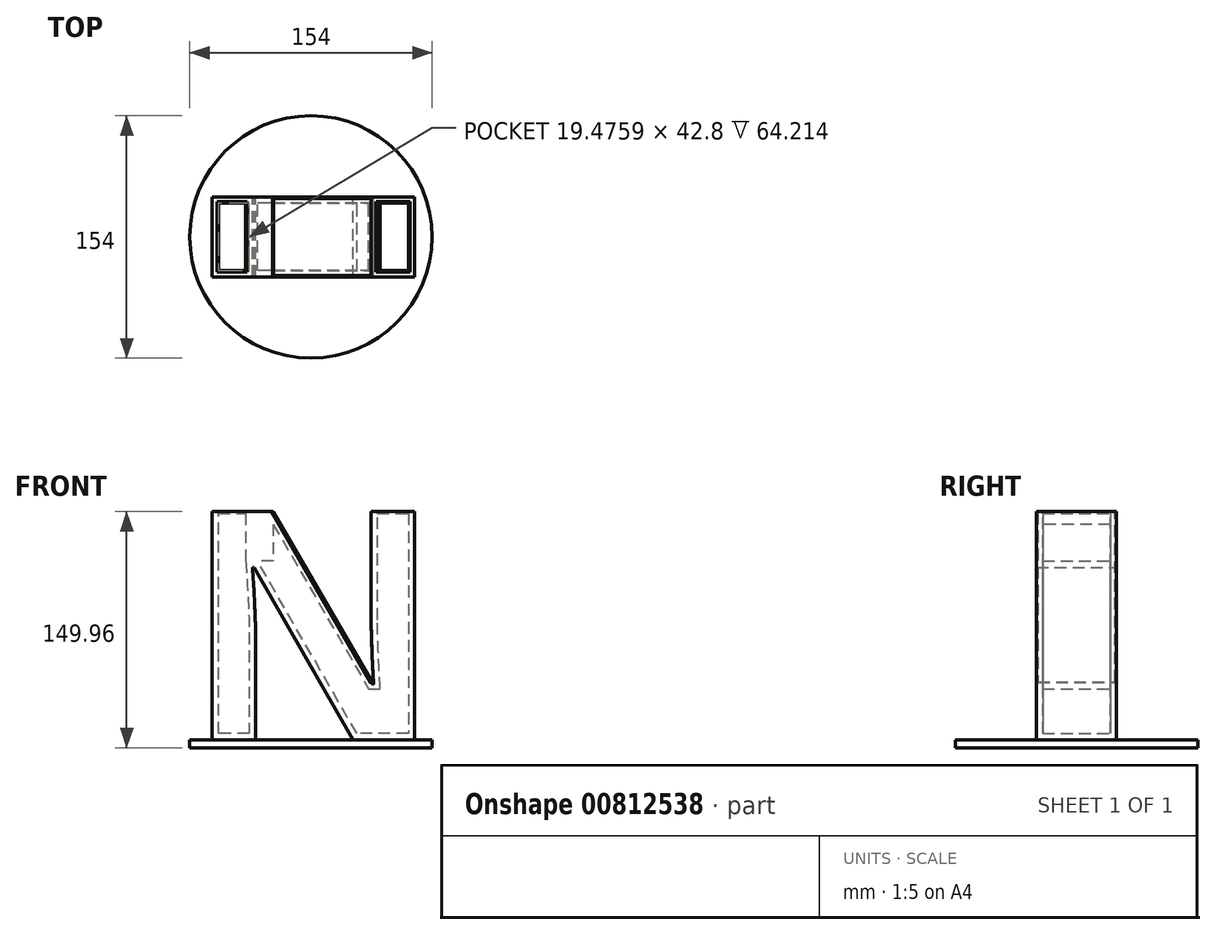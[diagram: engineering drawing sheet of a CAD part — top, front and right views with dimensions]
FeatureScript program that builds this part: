
annotation { "Feature Type Name" : "Feature", "Feature Type Description" : "" }
export const myFeature = defineFeature(function(context is Context, id is Id, definition is map)
    precondition{}
    {
        {
            var Q0;
            Q0=qCreatedBy(makeId("Top.planeOp"),FACE);
            var sketch = newSketch(context, id + "F0", { "sketchPlane" : qUnion([Q0])});
            skCircle(sketch, "E0", {"center": v(0, 0) * mm, "radius": 77 * mm});
            skSolve(sketch);
        }
        {
            var Q0;
            Q0=makeQuery(id+"F0.imprint","IMPRINT",FACE,{"disambiguationData":[TD([[makeQuery(id+"F0.imprint","IMPRINT",EDGE,{"derivedFrom":sQuery(id+"F0.wireOp",EDGE,"E0")}),1.0]])]});
            extrude(context, id + "F1", {"entities" : qUnion([Q0]), "oppositeDirection" : true, "depth" : 5 * mm, "offsetDistance" : 25 * mm});
        }
        {
            var Q0;
            Q0=qCreatedBy(makeId("Front.planeOp"),FACE);
            var sketch = newSketch(context, id + "F2", { "sketchPlane" : qUnion([Q0])});
            skText(sketch, "E1", { "text": "N", "fontName": "OpenSans-Bold.ttf"});
            const initialGuessF2  = {"E1": [-0.08095, 0, 1, 0, 0.1462]};
            skSetInitialGuess(sketch, initialGuessF2);
            skSolve(sketch);
        }
        {
            var Q0;
            Q0 = qSketchRegion(id + "F2", true);
            extrude(context, id + "F3", {"entities" : qUnion([Q0]), "endBound" : BoundingType.SYMMETRIC, "depth" : 50.8 * mm, "offsetDistance" : 25 * mm});
        }
        {
            var Q0;
            Q0=makeQuery(id+"F3.opExtrude","SWEPT_FACE",FACE,{"disambiguationData":[OSD([sQuery(id+"F2.wireOp",EDGE,"E1.sketch_text.stroke-7")])]});
            var Q1;
            Q1=makeQuery(id+"F3.opExtrude","SWEPT_FACE",FACE,{"disambiguationData":[OSD([sQuery(id+"F2.wireOp",EDGE,"E1.sketch_text.stroke-12")])]});
            shell(context, id + "F4", {"entities" : qUnion([Q0, Q1]), "thickness" : 4 * mm});
        }
        {
            var Q0;
            Q0=makeQuery(id+"F4.opShell","OFFSET_FACE",FACE,{"disambiguationData":[OSD([sQuery(id+"F2.wireOp",EDGE,"E1.sketch_text.stroke-2")])]});
            extrude(context, id + "F5", {"entities" : qUnion([Q0]), "operationType" : NewBodyOperationType.ADD, "depth" : 31.3 * mm, "offsetDistance" : 25 * mm});
        }
        {
            var Q0;
            Q0=makeQuery(id+"F5.opExtrude","SWEPT_FACE",FACE,{"disambiguationData":[OSD([sQuery(id+"F2.wireOp",EDGE,"E1.sketch_text.stroke-1"),sQuery(id+"F2.wireOp",EDGE,"E1.sketch_text.stroke-2")])]});
            extrude(context, id + "F6", {"entities" : qUnion([Q0]), "operationType" : NewBodyOperationType.ADD, "depth" : 10 * mm, "offsetDistance" : 25 * mm});
        }
        {
            var Q0;
            {var subQ0=sQuery(id+"F2.wireOp",EDGE,"E1.sketch_text.stroke-6");var subQ7=sQuery(id+"F2.wireOp",EDGE,"E1.sketch_text.stroke-7");Q0=makeQuery(id+"F5.boolean.opBoolean","SPLIT",EDGE,{"disambiguationData":[TD([makeQuery(id+"F4.opShell","OFFSET_FACE",FACE,{"disambiguationData":[OSD([subQ0])]})])],"derivedFrom":makeQuery(id+"F4.opShell","OFFSET_EDGE",EDGE,{"disambiguationData":[OSD([subQ7]),TDD([makeQuery(id+"F3.opExtrude","CAP_EDGE",EDGE,{"disambiguationData":[OSD([subQ7])],"isStart":true})])]})});}
            var Q1;
            Q1=makeQuery(id+"F5.opExtrude","CAP_EDGE",EDGE,{"disambiguationData":[OSD([sQuery(id+"F2.wireOp",EDGE,"E1.sketch_text.stroke-2"),sQuery(id+"F2.wireOp",EDGE,"E1.sketch_text.stroke-3")])],"isStart":false});
            var Q2;
            {var subQ0=sQuery(id+"F2.wireOp",EDGE,"E1.sketch_text.stroke-6");var subQ7=sQuery(id+"F2.wireOp",EDGE,"E1.sketch_text.stroke-7");Q2=makeQuery(id+"F5.boolean.opBoolean","SPLIT",EDGE,{"disambiguationData":[TD([makeQuery(id+"F4.opShell","OFFSET_FACE",FACE,{"disambiguationData":[OSD([subQ0])]})])],"derivedFrom":makeQuery(id+"F4.opShell","OFFSET_EDGE",EDGE,{"disambiguationData":[OSD([subQ7]),TDD([makeQuery(id+"F3.opExtrude","CAP_EDGE",EDGE,{"disambiguationData":[OSD([subQ7])],"isStart":false})])]})});}
            var Q3;
            Q3=makeQuery(id+"F4.opShell","OFFSET_EDGE",EDGE,{"disambiguationData":[OSD([sQuery(id+"F2.wireOp",EDGE,"E1.sketch_text.stroke-6"),sQuery(id+"F2.wireOp",EDGE,"E1.sketch_text.stroke-7")])]});
            var Q4;
            Q4=makeQuery(id+"F3.opExtrude","SWEPT_FACE",FACE,{"disambiguationData":[OSD([sQuery(id+"F2.wireOp",EDGE,"E1.sketch_text.stroke-8")])]});
            var Q5;
            Q5=makeQuery(id+"F4.opShell","OFFSET_EDGE",EDGE,{"disambiguationData":[OSD([sQuery(id+"F2.wireOp",EDGE,"E1.sketch_text.stroke-11"),sQuery(id+"F2.wireOp",EDGE,"E1.sketch_text.stroke-12")])]});
            var Q6;
            {var subQ0=sQuery(id+"F2.wireOp",EDGE,"E1.sketch_text.stroke-12");Q6=makeQuery(id+"F4.opShell","OFFSET_EDGE",EDGE,{"disambiguationData":[OSD([subQ0]),TDD([makeQuery(id+"F3.opExtrude","CAP_EDGE",EDGE,{"disambiguationData":[OSD([subQ0])],"isStart":true})])]});}
            var Q7;
            Q7=makeQuery(id+"F4.opShell","OFFSET_EDGE",EDGE,{"disambiguationData":[OSD([sQuery(id+"F2.wireOp",EDGE,"E1.sketch_text.stroke-12"),sQuery(id+"F2.wireOp",EDGE,"E1.sketch_text.stroke-13")])]});
            var Q8;
            {var subQ0=sQuery(id+"F2.wireOp",EDGE,"E1.sketch_text.stroke-12");Q8=makeQuery(id+"F4.opShell","OFFSET_EDGE",EDGE,{"disambiguationData":[OSD([subQ0]),TDD([makeQuery(id+"F3.opExtrude","CAP_EDGE",EDGE,{"disambiguationData":[OSD([subQ0])],"isStart":false})])]});}
            chamfer(context, id + "F7", {"entities" : qUnion([Q0, Q1, Q2, Q3, Q4, Q5, Q6, Q7, Q8]), "width" : 1 * mm, "tangentPropagation" : true});
        }
    });
